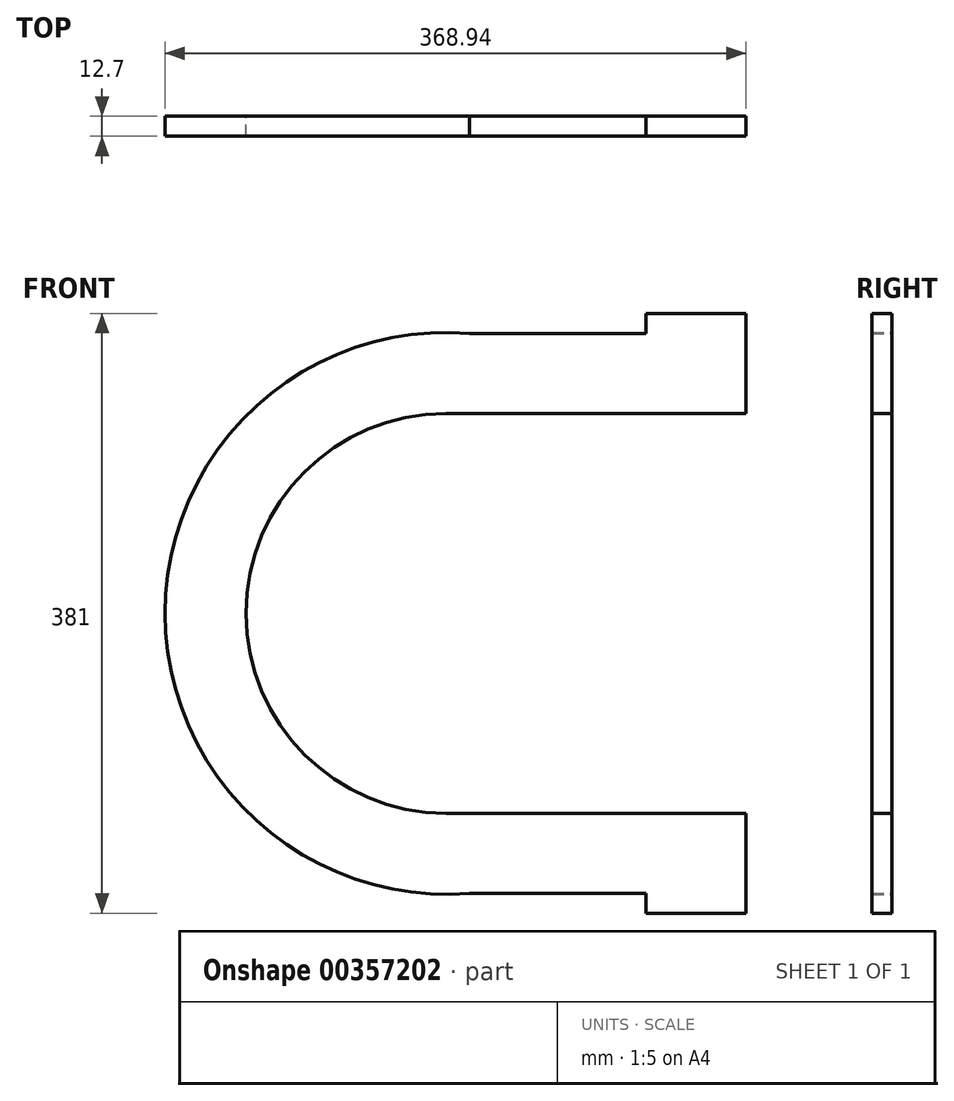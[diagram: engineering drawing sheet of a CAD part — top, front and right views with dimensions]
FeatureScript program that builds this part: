
annotation { "Feature Type Name" : "Feature", "Feature Type Description" : "" }
export const myFeature = defineFeature(function(context is Context, id is Id, definition is map)
    precondition{}
    {
        {
            var Q0;
            Q0=qCreatedBy(makeId("Front.planeOp"),FACE);
            var sketch = newSketch(context, id + "F0", { "sketchPlane" : qUnion([Q0])});
            skLineSegment(sketch, "E0.bottom", {"start": v(127, 177.8) * mm, "end": v(-15.05, 177.8) * mm});
            skLineSegment(sketch, "E0.top", {"start": v(127, -177.8) * mm, "end": v(-15.05, -177.8) * mm});
            skLineSegment(sketch, "E0.left", {"start": v(190.5, 177.8) * mm, "end": v(190.5, 127) * mm});
            skPoint(sketch, "E0.middle", {"position": v(0, 0) * mm});
            skArc(sketch, "E1", {"start": v(0, 127) * mm, "mid": v(-127, 0) * mm, "end": v(0, -127) * mm});
            skLineSegment(sketch, "E2", {"start": v(0, -127) * mm, "end": v(190.5, -127) * mm});
            skLineSegment(sketch, "E3", {"start": v(0, 127) * mm, "end": v(190.5, 127) * mm});
            skLineSegment(sketch, "E4.trimOffspring", {"start": v(190.5, -127) * mm, "end": v(190.5, -177.8) * mm});
            skArc(sketch, "E5", {"start": v(15.05, 177.8) * mm, "mid": v(-178.44, 0) * mm, "end": v(15.05, -177.8) * mm});
            skPoint(sketch, "E0.right.start.orphan", {"position": v(-190.5, 177.8) * mm});
            skPoint(sketch, "E6.orphan", {"position": v(-190.5, -177.8) * mm});
            skLineSegment(sketch, "E7.bottom", {"start": v(190.5, 127) * mm, "end": v(127, 127) * mm});
            skLineSegment(sketch, "E7.top", {"start": v(190.5, 190.5) * mm, "end": v(127, 190.5) * mm});
            skLineSegment(sketch, "E7.left", {"start": v(190.5, 127) * mm, "end": v(190.5, 190.5) * mm});
            skLineSegment(sketch, "E7.right", {"start": v(127, 177.8) * mm, "end": v(127, 190.5) * mm});
            skLineSegment(sketch, "E8.bottom", {"start": v(190.5, -127) * mm, "end": v(127, -127) * mm});
            skLineSegment(sketch, "E8.top", {"start": v(190.5, -190.5) * mm, "end": v(127, -190.5) * mm});
            skLineSegment(sketch, "E8.left", {"start": v(190.5, -127) * mm, "end": v(190.5, -190.5) * mm});
            skLineSegment(sketch, "E8.right", {"start": v(127, -177.8) * mm, "end": v(127, -190.5) * mm});
            skSolve(sketch);
        }
        {
            var Q0;
            Q0=qSketchRegion(id+"F0",true);
            extrude(context, id + "F1", {"entities" : qUnion([Q0]), "depth" : 12.7 * mm});
        }
    });
